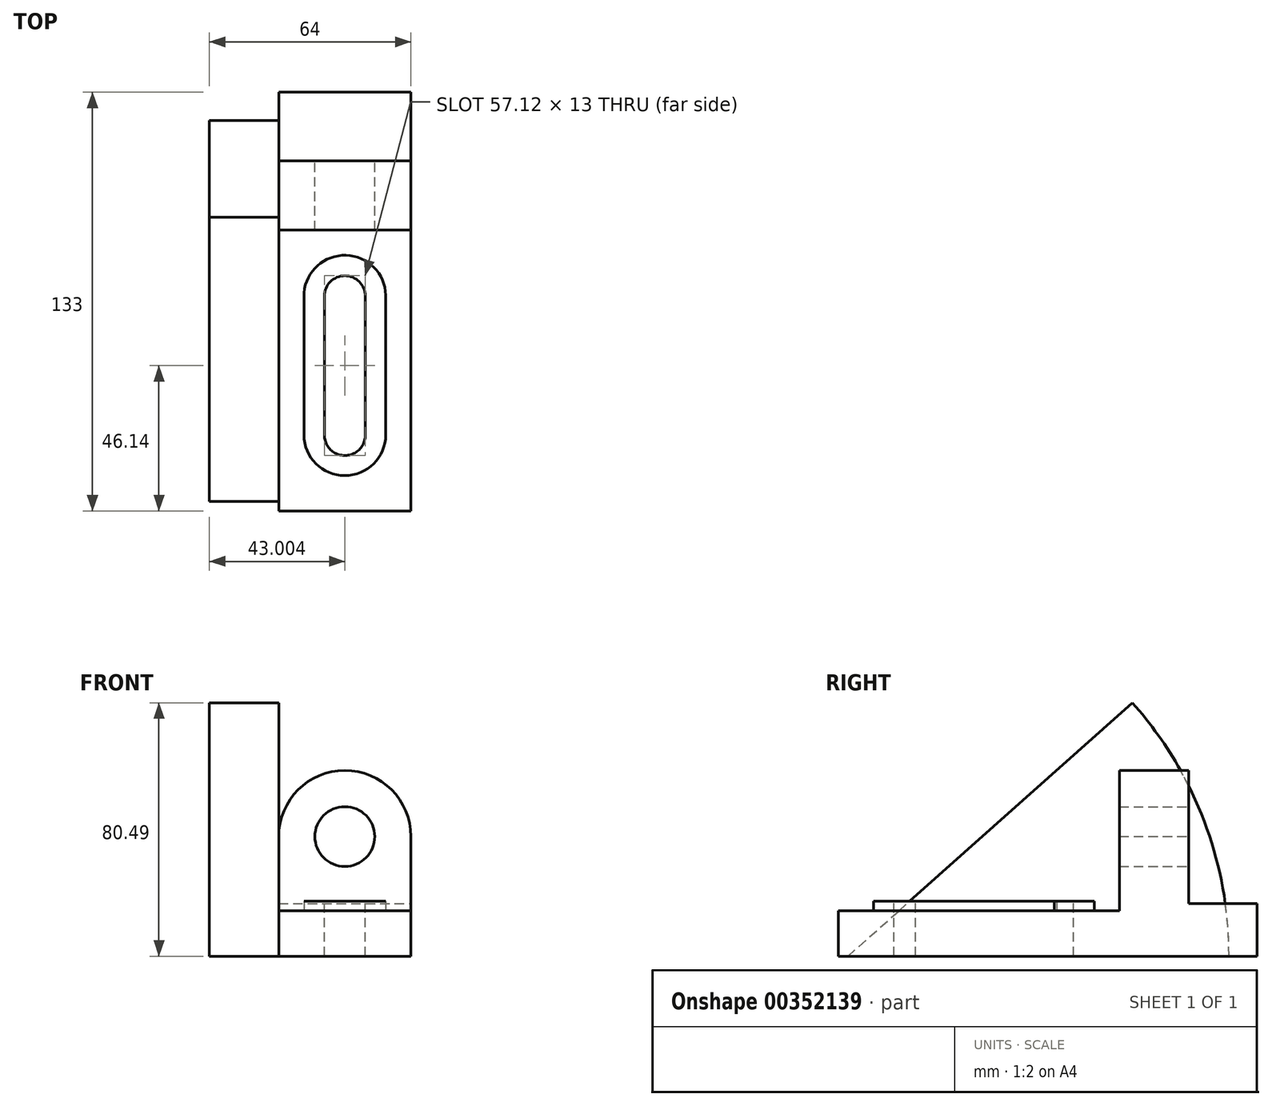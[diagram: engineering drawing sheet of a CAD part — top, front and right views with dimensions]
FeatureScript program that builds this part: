
annotation { "Feature Type Name" : "Feature", "Feature Type Description" : "" }
export const myFeature = defineFeature(function(context is Context, id is Id, definition is map)
    precondition{}
    {
        {
            var Q0;
            Q0=qCreatedBy(makeId("Front.planeOp"),FACE);
            var sketch = newSketch(context, id + "F0", { "sketchPlane" : qUnion([Q0])});
            skLineSegment(sketch, "E0", {"start": v(-23.64, 16) * mm, "end": v(-23.64, 0) * mm});
            skLineSegment(sketch, "E1", {"start": v(-23.64, 0) * mm, "end": v(18.36, 0) * mm});
            skLineSegment(sketch, "E2", {"start": v(18.36, 0) * mm, "end": v(18.36, 16) * mm});
            skLineSegment(sketch, "E3", {"start": v(18.36, 16) * mm, "end": v(-23.64, 16) * mm});
            skLineSegment(sketch, "E4", {"start": v(-23.64, 16) * mm, "end": v(-23.64, 38) * mm});
            skLineSegment(sketch, "E5", {"start": v(18.36, 38) * mm, "end": v(18.36, 16) * mm});
            skArc(sketch, "E6", {"start": v(18.36, 38) * mm, "mid": v(-2.64, 59) * mm, "end": v(-23.64, 38) * mm});
            skCircle(sketch, "E7", {"center": v(-2.64, 38) * mm, "radius": 9.5 * mm});
            skSolve(sketch);
        }
        {
            var Q0;
            Q0 = qSketchRegion(id + "F0", true);
            extrude(context, id + "F1", {"entities" : qUnion([Q0]), "depth" : 133 * mm});
        }
        {
            var Q0;
            Q0=qCreatedBy(makeId("Right.planeOp"),FACE);
            var sketch = newSketch(context, id + "F2", { "sketchPlane" : qUnion([Q0])});
            skLineSegment(sketch, "E8", {"start": v(-21.8, 66) * mm, "end": v(-21.8, 16.78) * mm});
            skLineSegment(sketch, "E9", {"start": v(-21.8, 16.78) * mm, "end": v(14.16, 16.78) * mm});
            skLineSegment(sketch, "E10", {"start": v(14.16, 16.78) * mm, "end": v(14.16, 66) * mm});
            skLineSegment(sketch, "E11", {"start": v(14.16, 66) * mm, "end": v(-21.8, 66) * mm});
            skLineSegment(sketch, "E12", {"start": v(-43.8, 68.55) * mm, "end": v(-43.8, 17.66) * mm});
            skLineSegment(sketch, "E13", {"start": v(-43.8, 17.66) * mm, "end": v(-134.39, 17.66) * mm});
            skLineSegment(sketch, "E14", {"start": v(-134.39, 17.66) * mm, "end": v(-134.39, 68.65) * mm});
            skLineSegment(sketch, "E15", {"start": v(-134.39, 68.65) * mm, "end": v(-43.8, 68.65) * mm});
            skSolve(sketch);
        }
        {
            var Q0;
            Q0 = qSketchRegion(id + "F2", true);
            extrude(context, id + "F3", {"entities" : qUnion([Q0]), "operationType" : NewBodyOperationType.REMOVE, "endBound" : BoundingType.THROUGH_ALL, "oppositeDirection" : true, "depth" : 25 * mm, "hasSecondDirection" : true, "secondDirectionOppositeDirection" : false, "secondDirectionDepth" : 25 * mm});
        }
        {
            var Q0;
            Q0=qCreatedBy(makeId("Right.planeOp"),FACE);
            var sketch = newSketch(context, id + "F4", { "sketchPlane" : qUnion([Q0])});
            skLineSegment(sketch, "E16", {"start": v(-43.8, 74.22) * mm, "end": v(-43.8, 14.46) * mm});
            skLineSegment(sketch, "E17", {"start": v(-43.8, 14.46) * mm, "end": v(-146.23, 14.46) * mm});
            skLineSegment(sketch, "E18", {"start": v(-146.23, 14.46) * mm, "end": v(-146.23, 74.22) * mm});
            skLineSegment(sketch, "E19", {"start": v(-146.23, 74.22) * mm, "end": v(-43.8, 74.22) * mm});
            skSolve(sketch);
        }
        {
            var Q0;
            Q0 = qSketchRegion(id + "F4", true);
            extrude(context, id + "F5", {"entities" : qUnion([Q0]), "operationType" : NewBodyOperationType.REMOVE, "oppositeDirection" : true, "depth" : 25 * mm, "hasSecondDirection" : true, "secondDirectionOppositeDirection" : false, "secondDirectionDepth" : 25 * mm});
        }
        {
            var Q0;
            Q0=makeQuery(id+"F1.opExtrude","SWEPT_FACE",FACE,{"disambiguationData":[OSD([sQuery(id+"F0.wireOp",EDGE,"E0"),sQuery(id+"F0.wireOp",EDGE,"E4")])]});
            var sketch = newSketch(context, id + "F6", { "sketchPlane" : qUnion([Q0])});
            skLineSegment(sketch, "E20", {"start": v(130, 0) * mm, "end": v(39.66, 80.5) * mm});
            skArc(sketch, "E21", {"start": v(39.66, 80.5) * mm, "mid": v(16.92, 43.07) * mm, "end": v(9, 0) * mm});
            skLineSegment(sketch, "E22", {"start": v(130, 0) * mm, "end": v(9, 0) * mm});
            skPoint(sketch, "E23.orphan", {"position": v(130, 121) * mm});
            skSolve(sketch);
        }
        {
            var Q0;
            Q0 = qSketchRegion(id + "F6", true);
            extrude(context, id + "F7", {"entities" : qUnion([Q0]), "operationType" : NewBodyOperationType.ADD, "depth" : 22 * mm});
        }
        {
            var Q0;
            Q0=makeQuery(id+"F5.boolean.opBoolean","COPY",FACE,{"derivedFrom":makeQuery(id+"F5.opExtrude","SWEPT_FACE",FACE,{"disambiguationData":[OSD([sQuery(id+"F4.wireOp",EDGE,"E17")])]})});
            var sketch = newSketch(context, id + "F8", { "sketchPlane" : qUnion([Q0])});
            skPoint(sketch, "E24", {"position": v(-2.64, -108.8) * mm});
            skPoint(sketch, "E25", {"position": v(-2.64, -64.8) * mm});
            skLineSegment(sketch, "E26", {"start": v(3.86, -64.8) * mm, "end": v(3.86, -108.48) * mm});
            skLineSegment(sketch, "E27", {"start": v(-9.14, -64.8) * mm, "end": v(-9.14, -108.92) * mm});
            skArc(sketch, "E28", {"start": v(3.86, -64.8) * mm, "mid": v(-2.64, -58.3) * mm, "end": v(-9.14, -64.8) * mm});
            skArc(sketch, "E29", {"start": v(-9.14, -108.92) * mm, "mid": v(-2.41, -115.42) * mm, "end": v(3.86, -108.48) * mm});
            skArc(sketch, "E30", {"start": v(10.36, -64.48) * mm, "mid": v(-2.26, -51.8) * mm, "end": v(-15.6, -63.72) * mm});
            skArc(sketch, "E31", {"start": v(-15.64, -108.92) * mm, "mid": v(-2.64, -121.8) * mm, "end": v(10.36, -108.92) * mm});
            skLineSegment(sketch, "E32", {"start": v(-15.6, -63.72) * mm, "end": v(-15.64, -108.92) * mm});
            skLineSegment(sketch, "E33", {"start": v(10.36, -64.48) * mm, "end": v(10.36, -108.92) * mm});
            skSolve(sketch);
        }
        {
            var Q0;
            Q0=makeQuery(id+"F8.imprint","IMPRINT",FACE,{"disambiguationData":[TD([[makeQuery(id+"F8.imprint","IMPRINT",EDGE,{"derivedFrom":sQuery(id+"F8.wireOp",EDGE,"E26")}),-1.0]])]});
            extrude(context, id + "F9", {"entities" : qUnion([Q0]), "operationType" : NewBodyOperationType.REMOVE, "oppositeDirection" : true, "depth" : 25 * mm});
        }
        {
            var Q0;
            Q0 = qSketchRegion(id + "F8", true);
            extrude(context, id + "F10", {"entities" : qUnion([Q0]), "operationType" : NewBodyOperationType.ADD, "depth" : 3 * mm});
        }
    });
